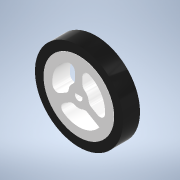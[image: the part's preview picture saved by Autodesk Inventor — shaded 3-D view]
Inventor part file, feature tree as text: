
AUTODESK INVENTOR PART (.ipt)
format: ipt  version: 2022.6 (Build 266554000, 554)  size: 189,440 bytes
history: native  units: mm
features: extrude x5, fillet x1, mirror x1
ambient origin geometry x8: Origin, YZ Plane, XZ Plane, XY Plane, X Axis, Y Axis, Z Axis, Center Point
bodies: Solid1 (feature_tree)
feature tree (7):
  extrude  "Extrusion1"  Depth=35.0mm
  extrude  "Extrusion2"  Depth=7.0mm TaperAngle=0.0deg
  fillet  "Fillet1"  Radius=21.0mm
  extrude  "Extrusion4"  Depth=8.0mm
  extrude  "Extrusion3"  Depth=3.0mm
  extrude  "Extrusion5"  Depth=30.0mm TaperAngle=360.0deg
  mirror  "Mirror1"
